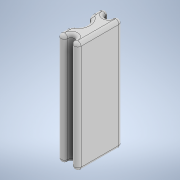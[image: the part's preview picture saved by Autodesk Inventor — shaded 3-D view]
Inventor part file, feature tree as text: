
AUTODESK INVENTOR PART (.ipt)
format: ipt  version: 2020 (Build 240168000, 168)  size: 189,952 bytes
history: native  units: in
note: dims shown in document units (in); Inventor stores cm internally (conversion verified against a paired STEP export)
features: fillet x3, extrude x1, sketch x1
ambient origin geometry x8: Origin, YZ Plane, XZ Plane, XY Plane, X Axis, Y Axis, Z Axis, Center Point
bodies: Solid1 (feature_tree)
feature tree (5):
  extrude  "Extrusion1"  Depth=0.0591in
  fillet  "Fillet1"  Radius=0.1181in
  fillet  "Fillet2"  Radius=0.1181in
  fillet  "Fillet3"  Radius=0.1181in
  sketch  "Sketch1"  dims[d0=0.1181in d1=0.7874in d2=0.1181in d3=0.1181in d4=0.1181in d5=0.1181in d6=0.2362in d7=0.1181in d8=0.2362in d9=0.1181in d10=1.9685in d11=0.0in d12=0.0591in d13=0.1181in d14=0.0591in]
